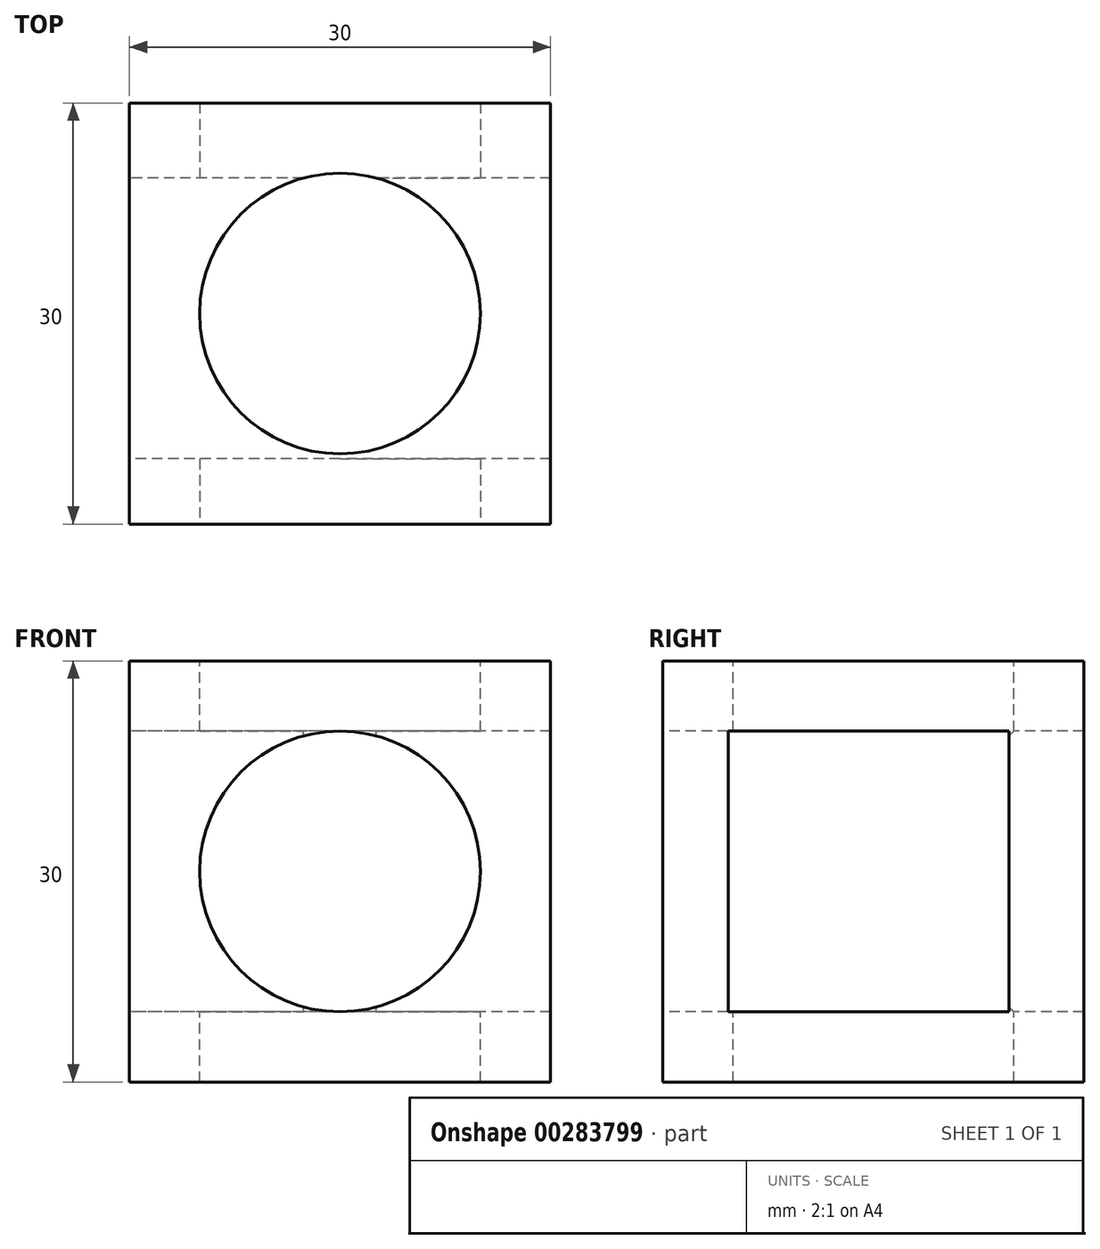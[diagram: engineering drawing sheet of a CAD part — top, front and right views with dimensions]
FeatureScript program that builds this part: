
annotation { "Feature Type Name" : "Feature", "Feature Type Description" : "" }
export const myFeature = defineFeature(function(context is Context, id is Id, definition is map)
    precondition{}
    {
        {
            var Q0;
            Q0=qCreatedBy(makeId("Front.planeOp"),FACE);
            var sketch = newSketch(context, id + "F0", { "sketchPlane" : qUnion([Q0])});
            skLineSegment(sketch, "E0.bottom", {"start": v(15, 15) * mm, "end": v(-15, 15) * mm});
            skLineSegment(sketch, "E0.top", {"start": v(15, -15) * mm, "end": v(-15, -15) * mm});
            skLineSegment(sketch, "E0.left", {"start": v(15, 15) * mm, "end": v(15, -15) * mm});
            skLineSegment(sketch, "E0.right", {"start": v(-15, 15) * mm, "end": v(-15, -15) * mm});
            skPoint(sketch, "E0.middle", {"position": v(0, 0) * mm});
            skSolve(sketch);
        }
        {
            var Q0;
            Q0=makeQuery(id+"F0.imprint","IMPRINT",FACE,{"disambiguationData":[TD([[makeQuery(id+"F0.imprint","IMPRINT",EDGE,{"derivedFrom":sQuery(id+"F0.wireOp",EDGE,"E0.bottom")}),1.0]])]});
            extrude(context, id + "F1", {"entities" : qUnion([Q0]), "depth" : 30 * mm});
        }
        {
            var Q0;
            Q0=makeQuery(id+"F1.opExtrude","SWEPT_FACE",FACE,{"disambiguationData":[OSD([sQuery(id+"F0.wireOp",EDGE,"E0.right")])]});
            var sketch = newSketch(context, id + "F2", { "sketchPlane" : qUnion([Q0])});
            skSolve(sketch);
        }
        {
            var Q0;
            Q0=makeQuery(id+"F1.opExtrude","CAP_FACE",FACE,{"disambiguationData":[OSD([sQuery(id+"F0.wireOp",EDGE,"E0.bottom"),sQuery(id+"F0.wireOp",EDGE,"E0.top"),sQuery(id+"F0.wireOp",EDGE,"E0.left"),sQuery(id+"F0.wireOp",EDGE,"E0.right")])],"isStart":false});
            var sketch = newSketch(context, id + "F3", { "sketchPlane" : qUnion([Q0])});
            skCircle(sketch, "E1", {"center": v(0, 0) * mm, "radius": 10 * mm});
            skSolve(sketch);
        }
        {
            var Q0;
            {var subQ0=sQuery(id+"F0.wireOp",EDGE,"E0.right");Q0=makeQuery(id+"F2.imprint","IMPRINT",FACE,{"disambiguationData":[TD([[makeQuery(id+"F2.imprint","IMPRINT",EDGE,{"derivedFrom":makeQuery(id+"F1.opExtrude","CAP_EDGE",EDGE,{"disambiguationData":[OSD([subQ0])],"isStart":true})}),1.0]])]});}
            var sketch = newSketch(context, id + "F4", { "sketchPlane" : qUnion([Q0])});
            skLineSegment(sketch, "E2.bottom", {"start": v(5.34, 10) * mm, "end": v(25.34, 10) * mm});
            skLineSegment(sketch, "E2.top", {"start": v(5.34, -10) * mm, "end": v(25.34, -10) * mm});
            skLineSegment(sketch, "E2.left", {"start": v(5.34, 10) * mm, "end": v(5.34, -10) * mm});
            skLineSegment(sketch, "E2.right", {"start": v(25.34, 10) * mm, "end": v(25.34, -10) * mm});
            skPoint(sketch, "E2.middle", {"position": v(15.34, 0) * mm});
            skSolve(sketch);
        }
        {
            var Q0;
            Q0 = qSketchRegion(id + "F3", true);
            extrude(context, id + "F5", {"entities" : qUnion([Q0]), "operationType" : NewBodyOperationType.REMOVE, "endBound" : BoundingType.THROUGH_ALL, "oppositeDirection" : true, "depth" : 25 * mm});
        }
        {
            var Q0;
            Q0=makeQuery(id+"F4.imprint","IMPRINT",FACE,{"disambiguationData":[TD([[makeQuery(id+"F4.imprint","IMPRINT",EDGE,{"derivedFrom":sQuery(id+"F4.wireOp",EDGE,"E2.bottom")}),-1.0]])]});
            extrude(context, id + "F6", {"entities" : qUnion([Q0]), "operationType" : NewBodyOperationType.REMOVE, "endBound" : BoundingType.THROUGH_ALL, "oppositeDirection" : true, "depth" : 25 * mm});
        }
        {
            var Q0;
            Q0=makeQuery(id+"F1.opExtrude","SWEPT_FACE",FACE,{"disambiguationData":[OSD([sQuery(id+"F0.wireOp",EDGE,"E0.bottom")])]});
            var sketch = newSketch(context, id + "F7", { "sketchPlane" : qUnion([Q0])});
            skCircle(sketch, "E3", {"center": v(0, -15) * mm, "radius": 10 * mm});
            skPoint(sketch, "E3.centerSnap0", {"position": v(15, -15) * mm});
            skPoint(sketch, "E3.centerSnap1", {"position": v(0, -30) * mm});
            skSolve(sketch);
        }
        {
            var Q0;
            Q0 = qSketchRegion(id + "F7", true);
            extrude(context, id + "F8", {"entities" : qUnion([Q0]), "operationType" : NewBodyOperationType.REMOVE, "endBound" : BoundingType.THROUGH_ALL, "oppositeDirection" : true, "depth" : 20 * mm});
        }
    });
